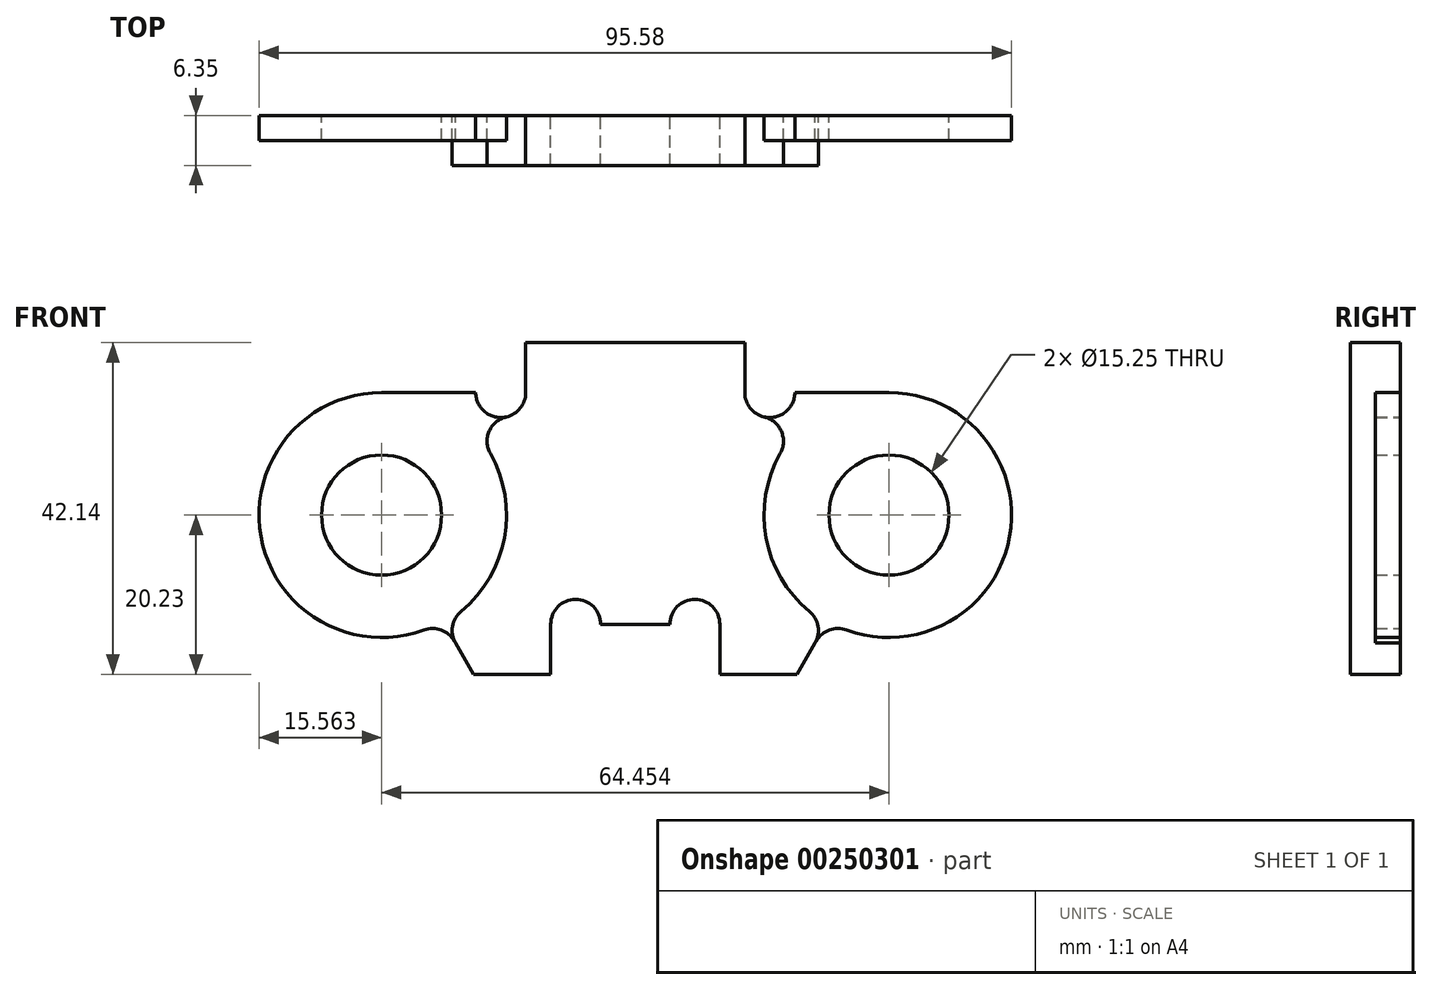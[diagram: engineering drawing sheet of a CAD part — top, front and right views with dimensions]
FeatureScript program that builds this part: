
annotation { "Feature Type Name" : "Feature", "Feature Type Description" : "" }
export const myFeature = defineFeature(function(context is Context, id is Id, definition is map)
    precondition{}
    {
        {
            var Q0;
            Q0=qCreatedBy(makeId("Front.planeOp"),FACE);
            var sketch = newSketch(context, id + "F0", { "sketchPlane" : qUnion([Q0])});
            skLineSegment(sketch, "E0", {"start": v(20.55, -20.23) * mm, "end": v(23, -16) * mm});
            skLineSegment(sketch, "E1", {"start": v(10.74, -20.23) * mm, "end": v(20.55, -20.23) * mm});
            skLineSegment(sketch, "E2", {"start": v(10.74, -13.88) * mm, "end": v(10.74, -20.23) * mm});
            skArc(sketch, "E3", {"start": v(10.74, -13.88) * mm, "mid": v(7.57, -10.7) * mm, "end": v(4.4, -13.88) * mm});
            skLineSegment(sketch, "E4", {"start": v(-4.4, -13.88) * mm, "end": v(4.4, -13.88) * mm});
            skArc(sketch, "E5", {"start": v(-4.4, -13.88) * mm, "mid": v(-7.57, -10.7) * mm, "end": v(-10.74, -13.88) * mm});
            skLineSegment(sketch, "E6", {"start": v(-10.74, -20.23) * mm, "end": v(-10.74, -13.88) * mm});
            skLineSegment(sketch, "E7", {"start": v(-20.55, -20.23) * mm, "end": v(-10.74, -20.23) * mm});
            skLineSegment(sketch, "E8", {"start": v(-23, -16) * mm, "end": v(-20.55, -20.23) * mm});
            skArc(sketch, "E9", {"start": v(-23, -16) * mm, "mid": v(-24.66, -14.6) * mm, "end": v(-26.84, -14.6) * mm});
            skArc(sketch, "E10", {"start": v(-32.23, 15.56) * mm, "mid": v(-47.55, -2.74) * mm, "end": v(-26.84, -14.6) * mm});
            skLineSegment(sketch, "E11", {"start": v(-20.27, 15.56) * mm, "end": v(-32.23, 15.56) * mm});
            skArc(sketch, "E12", {"start": v(-20.27, 15.56) * mm, "mid": v(-17.1, 12.39) * mm, "end": v(-13.92, 15.56) * mm});
            skLineSegment(sketch, "E13", {"start": v(-13.92, 21.91) * mm, "end": v(-13.92, 15.56) * mm});
            skLineSegment(sketch, "E14", {"start": v(13.92, 21.91) * mm, "end": v(-13.92, 21.91) * mm});
            skLineSegment(sketch, "E15", {"start": v(13.92, 15.56) * mm, "end": v(13.92, 21.91) * mm});
            skArc(sketch, "E16", {"start": v(13.92, 15.56) * mm, "mid": v(17.1, 12.39) * mm, "end": v(20.27, 15.56) * mm});
            skLineSegment(sketch, "E17", {"start": v(32.23, 15.56) * mm, "end": v(20.27, 15.56) * mm});
            skArc(sketch, "E18", {"start": v(26.84, -14.6) * mm, "mid": v(47.55, -2.74) * mm, "end": v(32.23, 15.56) * mm});
            skArc(sketch, "E19", {"start": v(26.84, -14.6) * mm, "mid": v(24.66, -14.6) * mm, "end": v(23, -16) * mm});
            skArc(sketch, "E20", {"start": v(-22.1, -12.23) * mm, "mid": v(-23.21, -14.12) * mm, "end": v(-22.84, -16.27) * mm});
            skArc(sketch, "E21", {"start": v(-16.37, 12.47) * mm, "mid": v(-18.55, 10.66) * mm, "end": v(-18.41, 7.82) * mm});
            skArc(sketch, "E22", {"start": v(-22.1, -12.23) * mm, "mid": v(-16.62, -2.88) * mm, "end": v(-18.41, 7.82) * mm});
            skCircle(sketch, "E23", {"center": v(32.23, 0) * mm, "radius": 7.63 * mm});
            skCircle(sketch, "E24", {"center": v(-32.23, 0) * mm, "radius": 7.63 * mm});
            skArc(sketch, "E25", {"start": v(18.41, 7.82) * mm, "mid": v(18.55, 10.66) * mm, "end": v(16.37, 12.47) * mm});
            skArc(sketch, "E26", {"start": v(18.41, 7.82) * mm, "mid": v(16.62, -2.88) * mm, "end": v(22.1, -12.23) * mm});
            skArc(sketch, "E27", {"start": v(22.84, -16.27) * mm, "mid": v(23.21, -14.12) * mm, "end": v(22.1, -12.23) * mm});
            skSolve(sketch);
        }
        {
            var Q0;
            {var subQ2=sQuery(id+"F0.wireOp",EDGE,"E9");Q0=makeQuery(id+"F0.imprint","IMPRINT",FACE,{"disambiguationData":[TD([[makeQuery(id+"F0.imprint","IMPRINT",EDGE,{"derivedFrom":subQ2}),-1.0]])]});}
            var Q1;
            {var subQ2=sQuery(id+"F0.wireOp",EDGE,"E17");Q1=makeQuery(id+"F0.imprint","IMPRINT",FACE,{"disambiguationData":[TD([[makeQuery(id+"F0.imprint","IMPRINT",EDGE,{"derivedFrom":subQ2}),1.0]])]});}
            extrude(context, id + "F1", {"entities" : qUnion([Q0, Q1]), "depth" : 3.17 * mm});
        }
        {
            var Q0;
            {var subQ4=sQuery(id+"F0.wireOp",EDGE,"E1");Q0=makeQuery(id+"F0.imprint","IMPRINT",FACE,{"disambiguationData":[TD([[makeQuery(id+"F0.imprint","IMPRINT",EDGE,{"derivedFrom":subQ4}),1.0]])]});}
            extrude(context, id + "F2", {"entities" : qUnion([Q0]), "depth" : 6.35 * mm});
        }
    });
